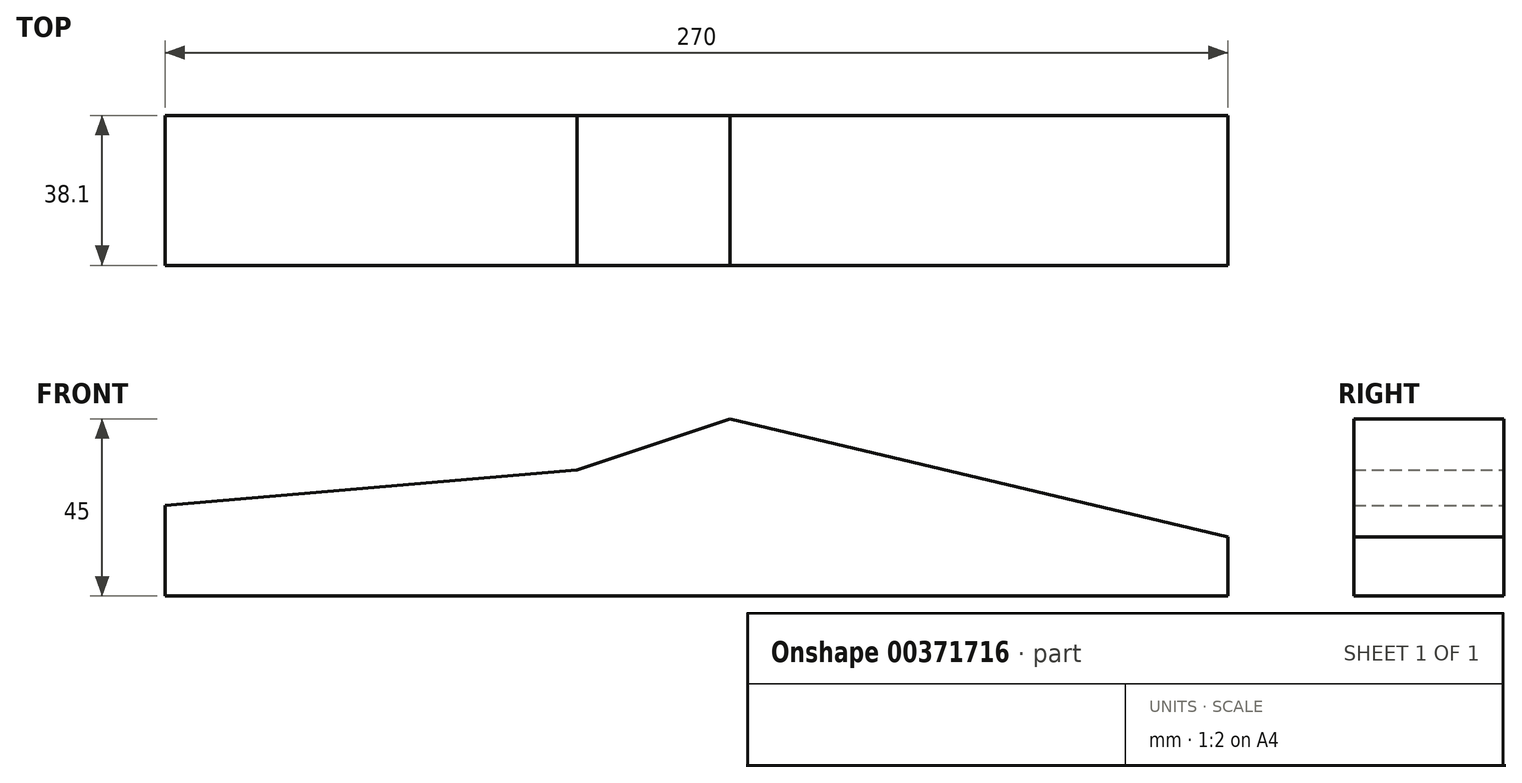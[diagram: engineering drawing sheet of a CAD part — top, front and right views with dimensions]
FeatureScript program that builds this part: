
annotation { "Feature Type Name" : "Feature", "Feature Type Description" : "" }
export const myFeature = defineFeature(function(context is Context, id is Id, definition is map)
    precondition{}
    {
        {
            var Q0;
            Q0=qCreatedBy(makeId("Front.planeOp"),FACE);
            var sketch = newSketch(context, id + "F0", { "sketchPlane" : qUnion([Q0])});
            skLineSegment(sketch, "E0", {"start": v(-143.5, 35.64) * mm, "end": v(126.5, 35.64) * mm});
            skLineSegment(sketch, "E1", {"start": v(-143.5, 35.64) * mm, "end": v(-143.5, 58.64) * mm});
            skLineSegment(sketch, "E2", {"start": v(-143.5, 58.64) * mm, "end": v(-38.9, 67.64) * mm});
            skLineSegment(sketch, "E3", {"start": v(-38.9, 67.64) * mm, "end": v(0, 80.64) * mm});
            skLineSegment(sketch, "E4", {"start": v(126.5, 35.64) * mm, "end": v(126.5, 50.64) * mm});
            skLineSegment(sketch, "E5", {"start": v(0, 80.64) * mm, "end": v(126.5, 50.64) * mm});
            skSolve(sketch);
        }
        {
            var Q0;
            Q0 = qSketchRegion(id + "F0", true);
            extrude(context, id + "F1", {"entities" : qUnion([Q0]), "endBound" : BoundingType.SYMMETRIC, "depth" : 38.1 * mm});
        }
    });
